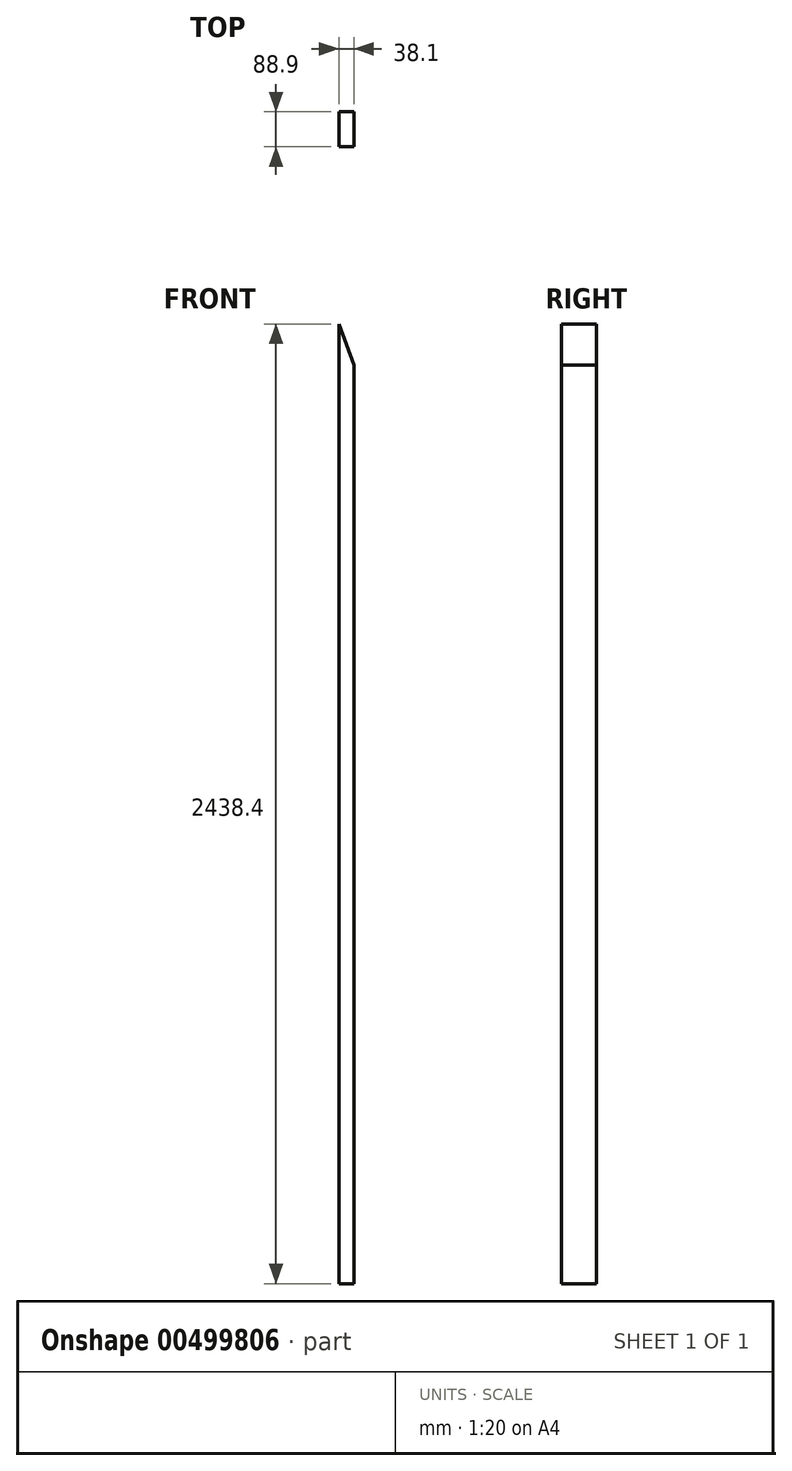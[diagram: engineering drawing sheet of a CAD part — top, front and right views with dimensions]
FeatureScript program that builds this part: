
annotation { "Feature Type Name" : "Feature", "Feature Type Description" : "" }
export const myFeature = defineFeature(function(context is Context, id is Id, definition is map)
    precondition{}
    {
        {
            var Q0;
            Q0=qCreatedBy(makeId("Front.planeOp"),FACE);
            var sketch = newSketch(context, id + "F0", { "sketchPlane" : qUnion([Q0])});
            skLineSegment(sketch, "E0.top", {"start": v(19.05, -1219.2) * mm, "end": v(-19.05, -1219.2) * mm});
            skLineSegment(sketch, "E0.left", {"start": v(19.05, 1114.52) * mm, "end": v(19.05, -1219.2) * mm});
            skLineSegment(sketch, "E0.right", {"start": v(-19.05, 1219.2) * mm, "end": v(-19.05, -1219.2) * mm});
            skPoint(sketch, "E0.middle", {"position": v(0, 0) * mm});
            skLineSegment(sketch, "E1", {"start": v(-19.05, 1219.2) * mm, "end": v(19.05, 1114.52) * mm});
            skPoint(sketch, "E2.orphan", {"position": v(19.05, 1219.2) * mm});
            skSolve(sketch);
        }
        {
            var Q0;
            Q0 = qSketchRegion(id + "F0", true);
            extrude(context, id + "F1", {"entities" : qUnion([Q0]), "depth" : 88.9 * mm});
        }
    });
